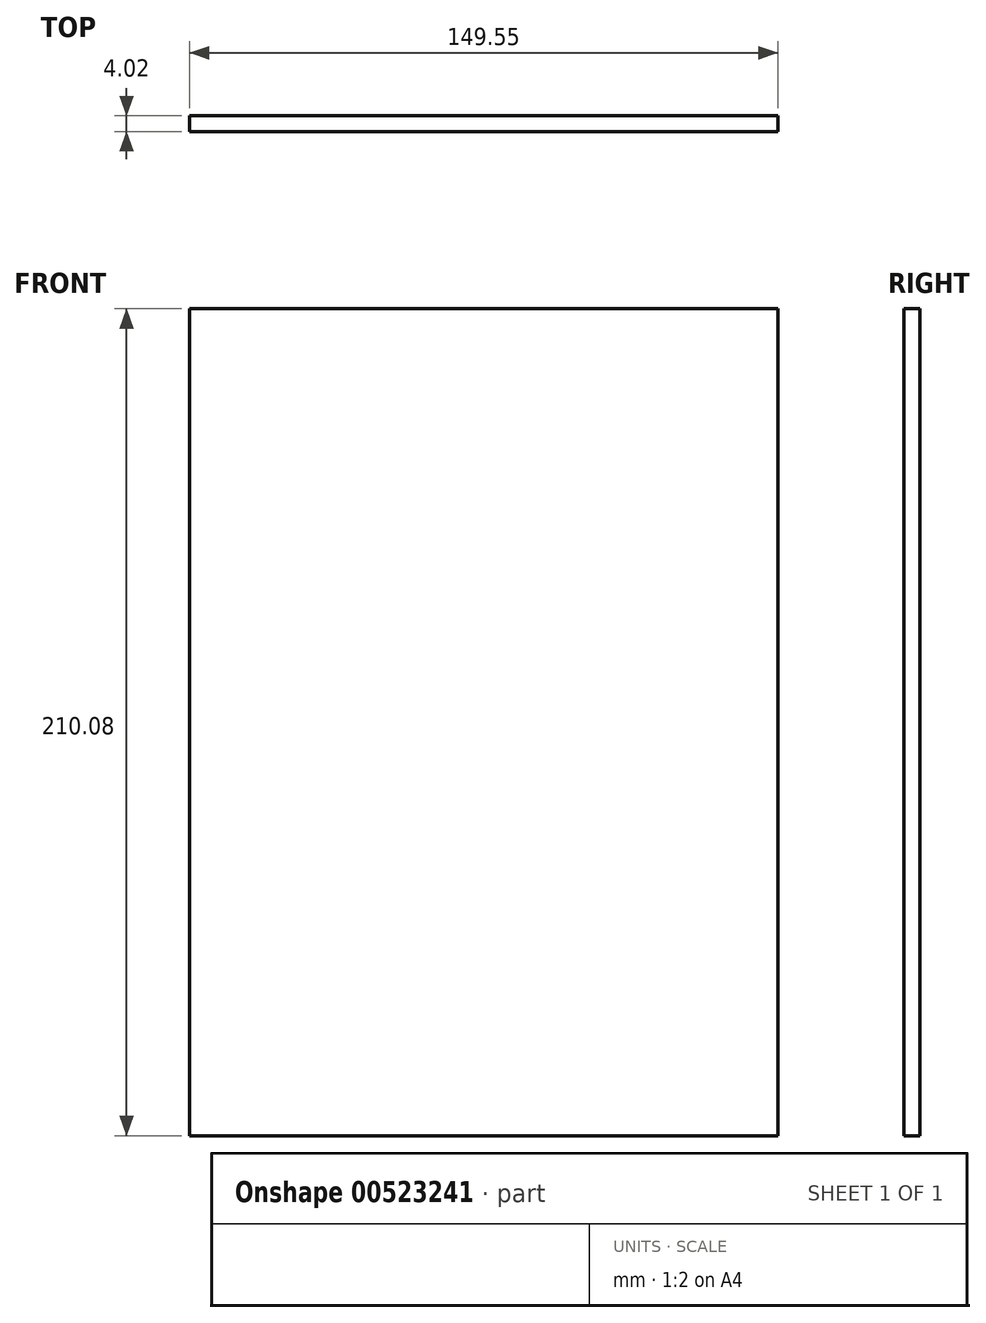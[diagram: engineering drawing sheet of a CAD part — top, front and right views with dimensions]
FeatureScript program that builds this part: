
annotation { "Feature Type Name" : "Feature", "Feature Type Description" : "" }
export const myFeature = defineFeature(function(context is Context, id is Id, definition is map)
    precondition{}
    {
        {
            var Q0;
            Q0=qCreatedBy(makeId("Front.planeOp"),FACE);
            var sketch = newSketch(context, id + "F0", { "sketchPlane" : qUnion([Q0])});
            skLineSegment(sketch, "E0.bottom", {"start": v(-58.2, 0) * mm, "end": v(91.34, 0) * mm});
            skLineSegment(sketch, "E0.top", {"start": v(-58.2, -210.08) * mm, "end": v(91.34, -210.08) * mm});
            skLineSegment(sketch, "E0.left", {"start": v(-58.2, 0) * mm, "end": v(-58.2, -210.08) * mm});
            skLineSegment(sketch, "E0.right", {"start": v(91.34, 0) * mm, "end": v(91.34, -210.08) * mm});
            skSolve(sketch);
        }
        {
            var Q0;
            Q0 = qSketchRegion(id + "F0", true);
            extrude(context, id + "F1", {"entities" : qUnion([Q0]), "depth" : 4.02 * mm, "offsetDistance" : 25.4 * mm});
        }
    });
